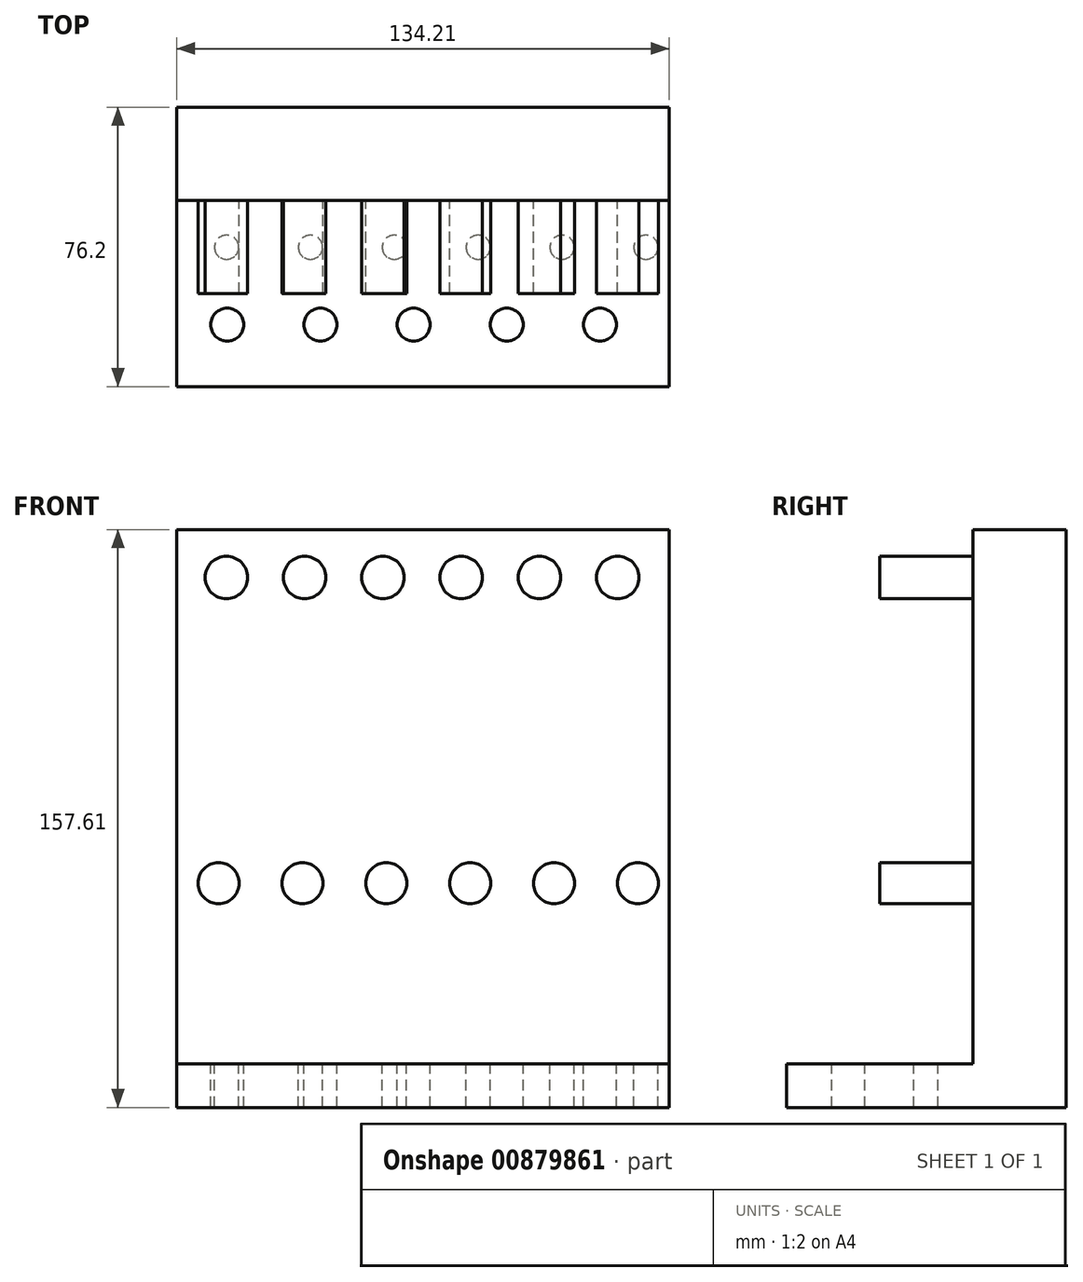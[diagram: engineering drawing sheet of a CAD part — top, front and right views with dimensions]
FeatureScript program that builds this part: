
annotation { "Feature Type Name" : "Feature", "Feature Type Description" : "" }
export const myFeature = defineFeature(function(context is Context, id is Id, definition is map)
    precondition{}
    {
        {
            var Q0;
            Q0=qCreatedBy(makeId("Front.planeOp"),FACE);
            var sketch = newSketch(context, id + "F0", { "sketchPlane" : qUnion([Q0])});
            skLineSegment(sketch, "E0", {"start": v(-68.74, 88.42) * mm, "end": v(65.47, 88.42) * mm});
            skLineSegment(sketch, "E1", {"start": v(65.47, 88.42) * mm, "end": v(65.47, -69.2) * mm});
            skLineSegment(sketch, "E2", {"start": v(65.47, -69.2) * mm, "end": v(-68.74, -69.2) * mm});
            skLineSegment(sketch, "E3", {"start": v(-68.74, -69.2) * mm, "end": v(-68.74, 88.42) * mm});
            skSolve(sketch);
        }
        {
            var Q0;
            Q0 = qSketchRegion(id + "F0", true);
            extrude(context, id + "F1", {"entities" : qUnion([Q0]), "depth" : 25.4 * mm, "offsetDistance" : 25.4 * mm});
        }
        {
            var Q0;
            Q0=makeQuery(id+"F1.opExtrude","CAP_FACE",FACE,{"disambiguationData":[OSD([sQuery(id+"F0.wireOp",EDGE,"E0"),sQuery(id+"F0.wireOp",EDGE,"E1"),sQuery(id+"F0.wireOp",EDGE,"E2"),sQuery(id+"F0.wireOp",EDGE,"E3")])],"isStart":false});
            var sketch = newSketch(context, id + "F2", { "sketchPlane" : qUnion([Q0])});
            skLineSegment(sketch, "E4", {"start": v(-68.74, -69.2) * mm, "end": v(65.47, -69.2) * mm});
            skLineSegment(sketch, "E5", {"start": v(65.47, -69.2) * mm, "end": v(65.47, -57.3) * mm});
            skLineSegment(sketch, "E6", {"start": v(65.47, -57.3) * mm, "end": v(-68.74, -57.3) * mm});
            skLineSegment(sketch, "E7", {"start": v(-68.74, -57.3) * mm, "end": v(-68.74, -69.2) * mm});
            skSolve(sketch);
        }
        {
            var Q0;
            Q0 = qSketchRegion(id + "F2", true);
            extrude(context, id + "F3", {"entities" : qUnion([Q0]), "operationType" : NewBodyOperationType.ADD, "depth" : 50.8 * mm, "offsetDistance" : 25.4 * mm});
        }
        {
            var Q0;
            Q0=makeQuery(id+"F3.opExtrude","SWEPT_FACE",FACE,{"disambiguationData":[OSD([sQuery(id+"F2.wireOp",EDGE,"E6")])]});
            var sketch = newSketch(context, id + "F4", { "sketchPlane" : qUnion([Q0])});
            skCircle(sketch, "E8", {"center": v(-55.16, -38.23) * mm, "radius": 3.3 * mm});
            skCircle(sketch, "E9.1.0.0", {"center": v(-32.3, -38.23) * mm, "radius": 3.3 * mm});
            skCircle(sketch, "E9.2.0.0", {"center": v(-9.44, -38.23) * mm, "radius": 3.3 * mm});
            skCircle(sketch, "E9.3.0.0", {"center": v(13.42, -38.23) * mm, "radius": 3.3 * mm});
            skCircle(sketch, "E9.4.0.0", {"center": v(36.28, -38.23) * mm, "radius": 3.3 * mm});
            skCircle(sketch, "E9.5.0.0", {"center": v(59.14, -38.23) * mm, "radius": 3.3 * mm});
            skLineSegment(sketch, "E9.direction1", {"start": v(-55.16, -38.23) * mm, "end": v(-32.3, -38.23) * mm, "construction": true});
            skCircle(sketch, "E10", {"center": v(-54.97, -59.33) * mm, "radius": 4.5 * mm});
            skCircle(sketch, "E11.1.0.0", {"center": v(-29.57, -59.33) * mm, "radius": 4.5 * mm});
            skCircle(sketch, "E11.2.0.0", {"center": v(-4.17, -59.33) * mm, "radius": 4.5 * mm});
            skCircle(sketch, "E11.3.0.0", {"center": v(21.23, -59.33) * mm, "radius": 4.5 * mm});
            skCircle(sketch, "E11.4.0.0", {"center": v(46.63, -59.33) * mm, "radius": 4.5 * mm});
            skLineSegment(sketch, "E11.direction1", {"start": v(-54.97, -59.33) * mm, "end": v(-29.57, -59.33) * mm, "construction": true});
            skSolve(sketch);
        }
        {
            var Q0;
            Q0 = qSketchRegion(id + "F4", true);
            extrude(context, id + "F5", {"entities" : qUnion([Q0]), "operationType" : NewBodyOperationType.REMOVE, "oppositeDirection" : true, "depth" : 25.4 * mm, "offsetDistance" : 25.4 * mm});
        }
        {
            var Q0;
            Q0=makeQuery(id+"F1.opExtrude","CAP_FACE",FACE,{"disambiguationData":[OSD([sQuery(id+"F0.wireOp",EDGE,"E0"),sQuery(id+"F0.wireOp",EDGE,"E1"),sQuery(id+"F0.wireOp",EDGE,"E2"),sQuery(id+"F0.wireOp",EDGE,"E3")])],"isStart":false});
            var sketch = newSketch(context, id + "F6", { "sketchPlane" : qUnion([Q0])});
            skCircle(sketch, "E12", {"center": v(-55.2, 75.32) * mm, "radius": 5.8 * mm});
            skCircle(sketch, "E13.1.0.0", {"center": v(-33.87, 75.32) * mm, "radius": 5.8 * mm});
            skCircle(sketch, "E13.2.0.0", {"center": v(-12.54, 75.32) * mm, "radius": 5.8 * mm});
            skCircle(sketch, "E13.3.0.0", {"center": v(8.8, 75.32) * mm, "radius": 5.8 * mm});
            skCircle(sketch, "E13.4.0.0", {"center": v(30.14, 75.32) * mm, "radius": 5.8 * mm});
            skCircle(sketch, "E13.5.0.0", {"center": v(51.47, 75.32) * mm, "radius": 5.8 * mm});
            skLineSegment(sketch, "E13.direction1", {"start": v(-55.2, 75.32) * mm, "end": v(-33.87, 75.32) * mm, "construction": true});
            skCircle(sketch, "E14", {"center": v(-57.33, -8.03) * mm, "radius": 5.59 * mm});
            skCircle(sketch, "E15.1.0.0", {"center": v(-34.47, -8.03) * mm, "radius": 5.59 * mm});
            skCircle(sketch, "E15.2.0.0", {"center": v(-11.6, -8.03) * mm, "radius": 5.59 * mm});
            skCircle(sketch, "E15.3.0.0", {"center": v(11.25, -8.03) * mm, "radius": 5.59 * mm});
            skCircle(sketch, "E15.4.0.0", {"center": v(34.11, -8.03) * mm, "radius": 5.59 * mm});
            skCircle(sketch, "E15.5.0.0", {"center": v(56.97, -8.03) * mm, "radius": 5.59 * mm});
            skLineSegment(sketch, "E15.direction1", {"start": v(-57.33, -8.03) * mm, "end": v(-34.47, -8.03) * mm, "construction": true});
            skSolve(sketch);
        }
        {
            var Q0;
            Q0 = qSketchRegion(id + "F6", true);
            extrude(context, id + "F7", {"entities" : qUnion([Q0]), "operationType" : NewBodyOperationType.ADD, "depth" : 25.4 * mm, "offsetDistance" : 25.4 * mm});
        }
    });
